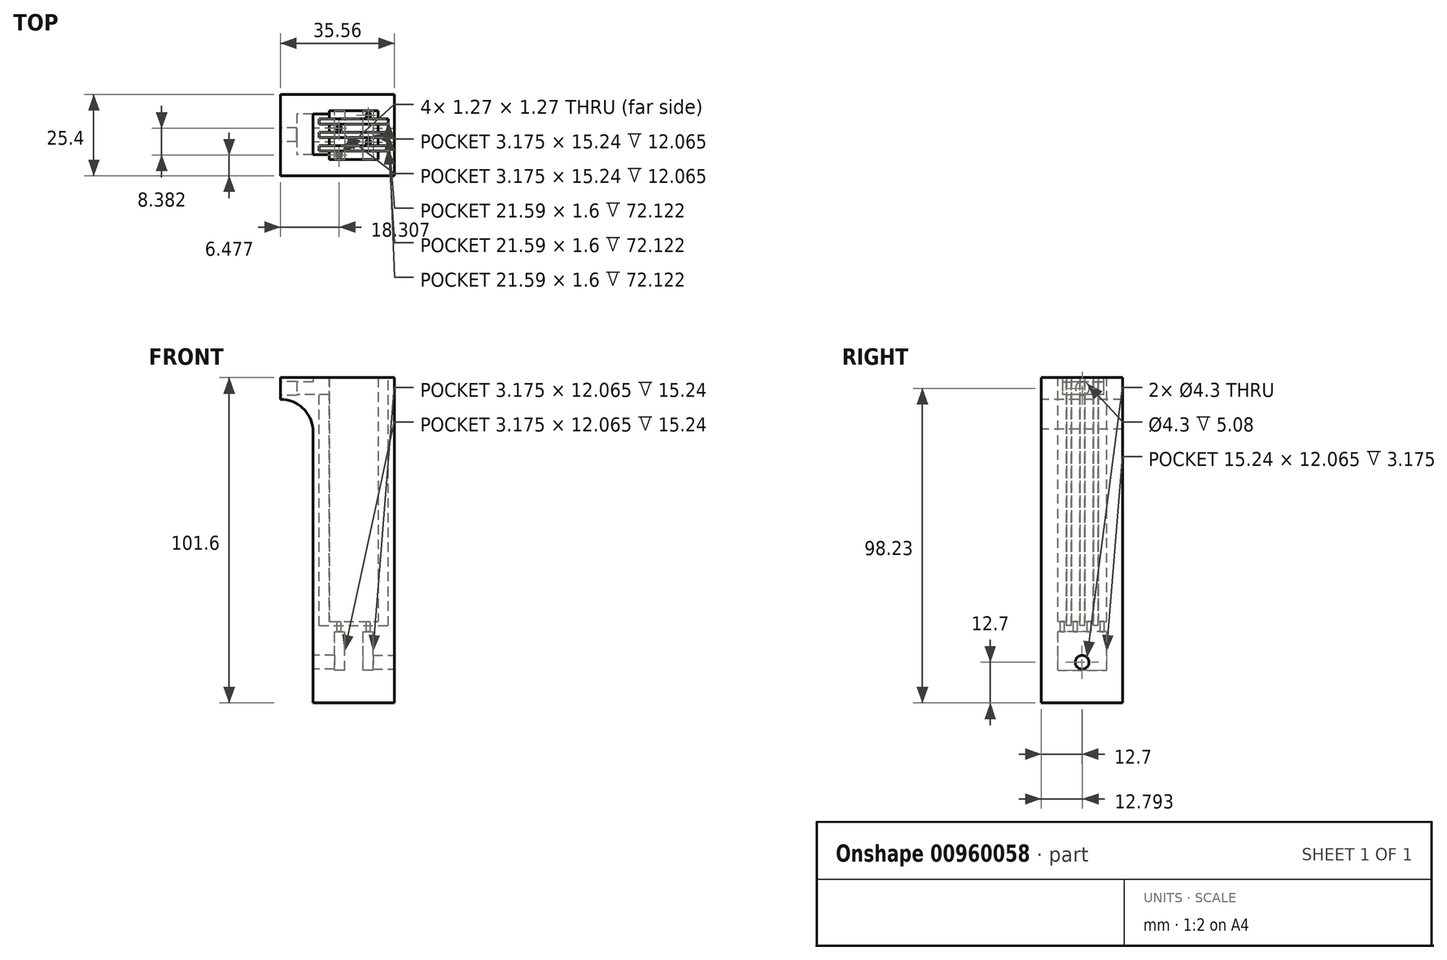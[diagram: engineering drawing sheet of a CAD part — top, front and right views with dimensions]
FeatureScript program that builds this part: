
annotation { "Feature Type Name" : "Feature", "Feature Type Description" : "" }
export const myFeature = defineFeature(function(context is Context, id is Id, definition is map)
    precondition{}
    {
        {
            var Q0;
            Q0=qCreatedBy(makeId("Top.planeOp"),FACE);
            var sketch = newSketch(context, id + "F0", { "sketchPlane" : qUnion([Q0])});
            skLineSegment(sketch, "E0.bottom", {"start": v(0, 0) * mm, "end": v(25.4, 0) * mm});
            skLineSegment(sketch, "E0.top", {"start": v(0, 25.4) * mm, "end": v(25.4, 25.4) * mm});
            skLineSegment(sketch, "E0.left", {"start": v(0, 0) * mm, "end": v(0, 25.4) * mm});
            skLineSegment(sketch, "E0.right", {"start": v(25.4, 0) * mm, "end": v(25.4, 25.4) * mm});
            skSolve(sketch);
        }
        {
            var Q0;
            Q0=makeQuery(id+"F0.imprint","IMPRINT",FACE,{"disambiguationData":[TD([[makeQuery(id+"F0.imprint","IMPRINT",EDGE,{"derivedFrom":sQuery(id+"F0.wireOp",EDGE,"E0.bottom")}),1.0]])]});
            extrude(context, id + "F1", {"entities" : qUnion([Q0]), "depth" : 101.6 * mm, "offsetDistance" : 25.4 * mm});
        }
        {
            var Q0;
            Q0=makeQuery(id+"F1.opExtrude","CAP_FACE",FACE,{"disambiguationData":[OSD([sQuery(id+"F0.wireOp",EDGE,"E0.bottom"),sQuery(id+"F0.wireOp",EDGE,"E0.top"),sQuery(id+"F0.wireOp",EDGE,"E0.left"),sQuery(id+"F0.wireOp",EDGE,"E0.right")])],"isStart":false});
            var sketch = newSketch(context, id + "F2", { "sketchPlane" : qUnion([Q0])});
            skLineSegment(sketch, "E1.bottom", {"start": v(5.08, 5.08) * mm, "end": v(20.32, 5.08) * mm});
            skLineSegment(sketch, "E1.top", {"start": v(5.08, 20.32) * mm, "end": v(20.32, 20.32) * mm});
            skLineSegment(sketch, "E1.left", {"start": v(5.08, 5.08) * mm, "end": v(5.08, 20.32) * mm});
            skLineSegment(sketch, "E1.right", {"start": v(20.32, 5.08) * mm, "end": v(20.32, 20.32) * mm});
            skSolve(sketch);
        }
        {
            var Q0;
            Q0=makeQuery(id+"F2.imprint","IMPRINT",FACE,{"disambiguationData":[TD([[makeQuery(id+"F2.imprint","IMPRINT",EDGE,{"derivedFrom":sQuery(id+"F2.wireOp",EDGE,"E1.bottom")}),1.0]])]});
            extrude(context, id + "F3", {"entities" : qUnion([Q0]), "operationType" : NewBodyOperationType.REMOVE, "oppositeDirection" : true, "depth" : 76.2 * mm, "offsetDistance" : 25.4 * mm});
        }
        {
            var Q0;
            Q0=makeQuery(id+"F1.opExtrude","SWEPT_FACE",FACE,{"disambiguationData":[OSD([sQuery(id+"F0.wireOp",EDGE,"E0.right")])]});
            var sketch = newSketch(context, id + "F4", { "sketchPlane" : qUnion([Q0])});
            skCircle(sketch, "E2", {"center": v(12.7, 12.7) * mm, "radius": 2.15 * mm});
            skSolve(sketch);
        }
        {
            var Q0;
            Q0=makeQuery(id+"F3.boolean.opBoolean","COPY",FACE,{"derivedFrom":makeQuery(id+"F3.opExtrude","CAP_FACE",FACE,{"disambiguationData":[OSD([sQuery(id+"F2.wireOp",EDGE,"E1.bottom"),sQuery(id+"F2.wireOp",EDGE,"E1.top"),sQuery(id+"F2.wireOp",EDGE,"E1.left"),sQuery(id+"F2.wireOp",EDGE,"E1.right")])],"isStart":false})});
            var sketch = newSketch(context, id + "F5", { "sketchPlane" : qUnion([Q0])});
            skLineSegment(sketch, "E3.bottom", {"start": v(15.56, 20.32) * mm, "end": v(18.73, 20.32) * mm});
            skLineSegment(sketch, "E3.top", {"start": v(15.56, 5.08) * mm, "end": v(18.73, 5.08) * mm});
            skLineSegment(sketch, "E3.left", {"start": v(15.56, 20.32) * mm, "end": v(15.56, 5.08) * mm});
            skLineSegment(sketch, "E3.right", {"start": v(18.73, 20.32) * mm, "end": v(18.73, 5.08) * mm});
            skLineSegment(sketch, "E4.bottom", {"start": v(6.67, 20.32) * mm, "end": v(9.84, 20.32) * mm});
            skLineSegment(sketch, "E4.top", {"start": v(6.67, 5.08) * mm, "end": v(9.84, 5.08) * mm});
            skLineSegment(sketch, "E4.left", {"start": v(6.67, 20.32) * mm, "end": v(6.67, 5.08) * mm});
            skLineSegment(sketch, "E4.right", {"start": v(9.84, 20.32) * mm, "end": v(9.84, 5.08) * mm});
            skSolve(sketch);
        }
        {
            var Q0;
            Q0=qSketchRegion(id+"F5",true);
            extrude(context, id + "F6", {"entities" : qUnion([Q0]), "operationType" : NewBodyOperationType.REMOVE, "endBound" : BoundingType.UP_TO_NEXT, "oppositeDirection" : true, "depth" : 25.4 * mm, "hasOffset" : true, "offsetDistance" : 10.16 * mm, "hasSecondDirection" : true, "secondDirectionOppositeDirection" : false, "secondDirectionDepth" : -3.17 * mm});
        }
        {
            var Q0;
            Q0=qSketchRegion(id+"F4",true);
            extrude(context, id + "F7", {"entities" : qUnion([Q0]), "operationType" : NewBodyOperationType.REMOVE, "endBound" : BoundingType.UP_TO_NEXT, "oppositeDirection" : true, "depth" : 25.4 * mm, "offsetDistance" : 25.4 * mm});
        }
        {
            var Q0;
            Q0=makeQuery(id+"F1.opExtrude","SWEPT_FACE",FACE,{"disambiguationData":[OSD([sQuery(id+"F0.wireOp",EDGE,"E0.left")])]});
            var sketch = newSketch(context, id + "F8", { "sketchPlane" : qUnion([Q0])});
            skCircle(sketch, "E5", {"center": v(-12.7, 12.7) * mm, "radius": 2.15 * mm});
            skSolve(sketch);
        }
        {
            var Q0;
            Q0=qSketchRegion(id+"F8",true);
            extrude(context, id + "F9", {"entities" : qUnion([Q0]), "operationType" : NewBodyOperationType.REMOVE, "endBound" : BoundingType.UP_TO_NEXT, "oppositeDirection" : true, "depth" : 25.4 * mm, "offsetDistance" : 25.4 * mm});
        }
        {
            var Q0;
            Q0=makeQuery(id+"F3.boolean.opBoolean","COPY",FACE,{"derivedFrom":makeQuery(id+"F3.opExtrude","CAP_FACE",FACE,{"disambiguationData":[OSD([sQuery(id+"F2.wireOp",EDGE,"E1.bottom"),sQuery(id+"F2.wireOp",EDGE,"E1.top"),sQuery(id+"F2.wireOp",EDGE,"E1.left"),sQuery(id+"F2.wireOp",EDGE,"E1.right")])],"isStart":false})});
            var sketch = newSketch(context, id + "F10", { "sketchPlane" : qUnion([Q0])});
            skLineSegment(sketch, "E6.bottom", {"start": v(16.57, 19.56) * mm, "end": v(17.84, 19.56) * mm});
            skLineSegment(sketch, "E6.top", {"start": v(16.57, 18.29) * mm, "end": v(17.84, 18.29) * mm});
            skLineSegment(sketch, "E6.left", {"start": v(16.57, 19.56) * mm, "end": v(16.57, 18.29) * mm});
            skLineSegment(sketch, "E6.right", {"start": v(17.84, 19.56) * mm, "end": v(17.84, 18.29) * mm});
            skLineSegment(sketch, "E7.0.1.0", {"start": v(16.57, 11.18) * mm, "end": v(17.84, 11.18) * mm});
            skLineSegment(sketch, "E7.0.1.1", {"start": v(17.84, 11.18) * mm, "end": v(17.84, 9.9) * mm});
            skLineSegment(sketch, "E7.0.1.2", {"start": v(16.57, 9.9) * mm, "end": v(17.84, 9.9) * mm});
            skLineSegment(sketch, "E7.0.1.3", {"start": v(16.57, 11.18) * mm, "end": v(16.57, 9.9) * mm});
            skLineSegment(sketch, "E7.direction1", {"start": v(16.57, 18.29) * mm, "end": v(41.97, 18.29) * mm, "construction": true});
            skLineSegment(sketch, "E7.direction2", {"start": v(16.57, 18.29) * mm, "end": v(16.57, 9.9) * mm, "construction": true});
            skSolve(sketch);
        }
        {
            var Q0;
            Q0=makeQuery(id+"F10.imprint","IMPRINT",FACE,{"disambiguationData":[TD([[makeQuery(id+"F10.imprint","IMPRINT",EDGE,{"derivedFrom":sQuery(id+"F10.wireOp",EDGE,"E6.bottom")}),1.0]])]});
            var sketch = newSketch(context, id + "F11", { "sketchPlane" : qUnion([Q0])});
            skLineSegment(sketch, "E8.bottom", {"start": v(7.51, 7.11) * mm, "end": v(8.78, 7.11) * mm});
            skLineSegment(sketch, "E8.top", {"start": v(7.51, 5.84) * mm, "end": v(8.78, 5.84) * mm});
            skLineSegment(sketch, "E8.left", {"start": v(7.51, 7.11) * mm, "end": v(7.51, 5.84) * mm});
            skLineSegment(sketch, "E8.right", {"start": v(8.78, 7.11) * mm, "end": v(8.78, 5.84) * mm});
            skLineSegment(sketch, "E9.bottom", {"start": v(7.51, 15.5) * mm, "end": v(8.78, 15.5) * mm});
            skLineSegment(sketch, "E9.top", {"start": v(7.51, 14.22) * mm, "end": v(8.78, 14.22) * mm});
            skLineSegment(sketch, "E9.left", {"start": v(7.51, 15.5) * mm, "end": v(7.51, 14.22) * mm});
            skLineSegment(sketch, "E9.right", {"start": v(8.78, 15.5) * mm, "end": v(8.78, 14.22) * mm});
            skSolve(sketch);
        }
        {
            var Q0;
            Q0=qSketchRegion(id+"F10",true);
            extrude(context, id + "F12", {"entities" : qUnion([Q0]), "operationType" : NewBodyOperationType.REMOVE, "endBound" : BoundingType.UP_TO_NEXT, "oppositeDirection" : true, "depth" : 25.4 * mm, "offsetDistance" : 25.4 * mm});
        }
        {
            var Q0;
            Q0=qSketchRegion(id+"F11",true);
            extrude(context, id + "F13", {"entities" : qUnion([Q0]), "operationType" : NewBodyOperationType.REMOVE, "endBound" : BoundingType.UP_TO_NEXT, "oppositeDirection" : true, "depth" : 25.4 * mm, "offsetDistance" : 25.4 * mm});
        }
        {
            var Q0;
            Q0=makeQuery(id+"F1.opExtrude","SWEPT_FACE",FACE,{"disambiguationData":[OSD([sQuery(id+"F0.wireOp",EDGE,"E0.left")])]});
            var sketch = newSketch(context, id + "F14", { "sketchPlane" : qUnion([Q0])});
            skLineSegment(sketch, "E10.bottom", {"start": v(-19.33, 100.27) * mm, "end": v(-6.55, 100.27) * mm});
            skLineSegment(sketch, "E10.top", {"start": v(-19.33, 96.25) * mm, "end": v(-6.55, 96.25) * mm});
            skLineSegment(sketch, "E10.left", {"start": v(-19.33, 100.27) * mm, "end": v(-19.33, 96.25) * mm});
            skLineSegment(sketch, "E10.right", {"start": v(-6.55, 100.27) * mm, "end": v(-6.55, 96.25) * mm});
            skSolve(sketch);
        }
        {
            var Q0;
            Q0=qSketchRegion(id+"F14",true);
            extrude(context, id + "F15", {"entities" : qUnion([Q0]), "operationType" : NewBodyOperationType.REMOVE, "endBound" : BoundingType.UP_TO_NEXT, "oppositeDirection" : true, "depth" : 25.4 * mm, "offsetDistance" : 25.4 * mm});
        }
        {
            var Q0;
            Q0=makeQuery(id+"F1.opExtrude","SWEPT_FACE",FACE,{"disambiguationData":[OSD([sQuery(id+"F0.wireOp",EDGE,"E0.left")])]});
            var sketch = newSketch(context, id + "F16", { "sketchPlane" : qUnion([Q0])});
            skLineSegment(sketch, "E11.bottom", {"start": v(-25.4, 101.6) * mm, "end": v(0, 101.6) * mm});
            skLineSegment(sketch, "E11.top", {"start": v(-25.4, 94.82) * mm, "end": v(0, 94.82) * mm});
            skLineSegment(sketch, "E11.left", {"start": v(-25.4, 101.6) * mm, "end": v(-25.4, 94.82) * mm});
            skLineSegment(sketch, "E11.right", {"start": v(0, 101.6) * mm, "end": v(0, 94.82) * mm});
            skSolve(sketch);
        }
        {
            var Q0;
            Q0=makeQuery(id+"F16.imprint","IMPRINT",FACE,{"disambiguationData":[TD([[makeQuery(id+"F16.imprint","IMPRINT",EDGE,{"derivedFrom":sQuery(id+"F16.wireOp",EDGE,"E11.bottom")}),1.0]])]});
            extrude(context, id + "F17", {"entities" : qUnion([Q0]), "operationType" : NewBodyOperationType.ADD, "depth" : 5.08 * mm, "offsetDistance" : 25.4 * mm});
        }
        {
            var Q0;
            Q0=makeQuery(id+"F17.opExtrude","CAP_FACE",FACE,{"disambiguationData":[OSD([sQuery(id+"F14.wireOp",EDGE,"E10.bottom"),sQuery(id+"F14.wireOp",EDGE,"E10.top"),sQuery(id+"F14.wireOp",EDGE,"E10.left"),sQuery(id+"F14.wireOp",EDGE,"E10.right"),sQuery(id+"F16.wireOp",EDGE,"E11.bottom"),sQuery(id+"F16.wireOp",EDGE,"E11.top"),sQuery(id+"F16.wireOp",EDGE,"E11.left"),sQuery(id+"F16.wireOp",EDGE,"E11.right")])],"isStart":false});
            var sketch = newSketch(context, id + "F18", { "sketchPlane" : qUnion([Q0])});
            skLineSegment(sketch, "E12.bottom", {"start": v(-25.4, 101.6) * mm, "end": v(0, 101.6) * mm});
            skLineSegment(sketch, "E12.top", {"start": v(-25.4, 94.82) * mm, "end": v(0, 94.82) * mm});
            skLineSegment(sketch, "E12.left", {"start": v(-25.4, 101.6) * mm, "end": v(-25.4, 94.82) * mm});
            skLineSegment(sketch, "E12.right", {"start": v(0, 101.6) * mm, "end": v(0, 94.82) * mm});
            skSolve(sketch);
        }
        {
            var Q0;
            Q0=qSketchRegion(id+"F18",true);
            extrude(context, id + "F19", {"entities" : qUnion([Q0]), "operationType" : NewBodyOperationType.ADD, "depth" : 5.08 * mm, "offsetDistance" : 25.4 * mm});
        }
        {
            var Q0;
            Q0=makeQuery(id+"F19.opExtrude","CAP_FACE",FACE,{"disambiguationData":[OSD([sQuery(id+"F18.wireOp",EDGE,"E12.bottom"),sQuery(id+"F18.wireOp",EDGE,"E12.top"),sQuery(id+"F18.wireOp",EDGE,"E12.left"),sQuery(id+"F18.wireOp",EDGE,"E12.right")])],"isStart":false});
            var sketch = newSketch(context, id + "F20", { "sketchPlane" : qUnion([Q0])});
            skCircle(sketch, "E13", {"center": v(-12.8, 98.23) * mm, "radius": 2.15 * mm});
            skSolve(sketch);
        }
        {
            var Q0;
            Q0=qSketchRegion(id+"F20",true);
            extrude(context, id + "F21", {"entities" : qUnion([Q0]), "operationType" : NewBodyOperationType.REMOVE, "oppositeDirection" : true, "depth" : 5.08 * mm, "offsetDistance" : 25.4 * mm});
        }
        {
            var Q0;
            Q0=makeQuery(id+"F19.boolean.opBoolean","MERGE",FACE,{"derivedFrom":[makeQuery(id+"F17.boolean.opBoolean","MERGE",FACE,{"derivedFrom":[makeQuery(id+"F1.opExtrude","SWEPT_FACE",FACE,{"disambiguationData":[OSD([sQuery(id+"F0.wireOp",EDGE,"E0.bottom")])]}),makeQuery(id+"F17.opExtrude","SWEPT_FACE",FACE,{"disambiguationData":[OSD([sQuery(id+"F16.wireOp",EDGE,"E11.right")])]})]}),makeQuery(id+"F19.opExtrude","SWEPT_FACE",FACE,{"disambiguationData":[OSD([sQuery(id+"F18.wireOp",EDGE,"E12.right")])]})]});
            var sketch = newSketch(context, id + "F22", { "sketchPlane" : qUnion([Q0])});
            skArc(sketch, "E14", {"start": v(0, 85.44) * mm, "mid": v(-3.25, 92.12) * mm, "end": v(-10.16, 94.82) * mm});
            skLineSegment(sketch, "E15", {"start": v(-10.16, 94.82) * mm, "end": v(0, 94.82) * mm});
            skLineSegment(sketch, "E16", {"start": v(0, 94.82) * mm, "end": v(0, 85.44) * mm});
            skSolve(sketch);
        }
        {
            var Q0;
            Q0 = qSketchRegion(id + "F22", true);
            var Q1;
            Q1=makeQuery(id+"F19.boolean.opBoolean","MERGE",FACE,{"derivedFrom":[makeQuery(id+"F17.boolean.opBoolean","MERGE",FACE,{"derivedFrom":[makeQuery(id+"F1.opExtrude","SWEPT_FACE",FACE,{"disambiguationData":[OSD([sQuery(id+"F0.wireOp",EDGE,"E0.top")])]}),makeQuery(id+"F17.opExtrude","SWEPT_FACE",FACE,{"disambiguationData":[OSD([sQuery(id+"F16.wireOp",EDGE,"E11.left")])]})]}),makeQuery(id+"F19.opExtrude","SWEPT_FACE",FACE,{"disambiguationData":[OSD([sQuery(id+"F18.wireOp",EDGE,"E12.left")])]})]});
            extrude(context, id + "F23", {"entities" : qUnion([Q0]), "operationType" : NewBodyOperationType.ADD, "endBound" : BoundingType.UP_TO_SURFACE, "oppositeDirection" : true, "depth" : 25.4 * mm, "endBoundEntityFace" : qUnion([Q1]), "offsetDistance" : 25.4 * mm});
        }
        {
            var Q0;
            Q0=makeQuery(id+"F19.boolean.opBoolean","MERGE",FACE,{"derivedFrom":[makeQuery(id+"F17.boolean.opBoolean","MERGE",FACE,{"derivedFrom":[makeQuery(id+"F1.opExtrude","CAP_FACE",FACE,{"disambiguationData":[OSD([sQuery(id+"F0.wireOp",EDGE,"E0.bottom"),sQuery(id+"F0.wireOp",EDGE,"E0.top"),sQuery(id+"F0.wireOp",EDGE,"E0.left"),sQuery(id+"F0.wireOp",EDGE,"E0.right")])],"isStart":false}),makeQuery(id+"F17.opExtrude","SWEPT_FACE",FACE,{"disambiguationData":[OSD([sQuery(id+"F16.wireOp",EDGE,"E11.bottom")])]})]}),makeQuery(id+"F19.opExtrude","SWEPT_FACE",FACE,{"disambiguationData":[OSD([sQuery(id+"F18.wireOp",EDGE,"E12.bottom")])]})]});
            var sketch = newSketch(context, id + "F24", { "sketchPlane" : qUnion([Q0])});
            skLineSegment(sketch, "E17.bottom", {"start": v(1.9, 17.74) * mm, "end": v(23.5, 17.74) * mm});
            skLineSegment(sketch, "E17.top", {"start": v(1.9, 16.14) * mm, "end": v(23.5, 16.14) * mm});
            skLineSegment(sketch, "E17.left", {"start": v(1.9, 17.74) * mm, "end": v(1.9, 16.14) * mm});
            skLineSegment(sketch, "E17.right", {"start": v(23.5, 17.74) * mm, "end": v(23.5, 16.14) * mm});
            skLineSegment(sketch, "E18.bottom", {"start": v(1.9, 9.37) * mm, "end": v(23.5, 9.37) * mm});
            skLineSegment(sketch, "E18.top", {"start": v(1.9, 7.77) * mm, "end": v(23.5, 7.77) * mm});
            skLineSegment(sketch, "E18.left", {"start": v(1.9, 9.37) * mm, "end": v(1.9, 7.77) * mm});
            skLineSegment(sketch, "E18.right", {"start": v(23.5, 9.37) * mm, "end": v(23.5, 7.77) * mm});
            skLineSegment(sketch, "E19.bottom", {"start": v(1.9, 13.55) * mm, "end": v(23.5, 13.55) * mm});
            skLineSegment(sketch, "E19.top", {"start": v(1.9, 11.95) * mm, "end": v(23.5, 11.95) * mm});
            skLineSegment(sketch, "E19.left", {"start": v(1.9, 13.55) * mm, "end": v(1.9, 11.95) * mm});
            skLineSegment(sketch, "E19.right", {"start": v(23.5, 13.55) * mm, "end": v(23.5, 11.95) * mm});
            skSolve(sketch);
        }
        {
            var Q0;
            Q0 = qSketchRegion(id + "F24", true);
            extrude(context, id + "F25", {"entities" : qUnion([Q0]), "operationType" : NewBodyOperationType.REMOVE, "oppositeDirection" : true, "depth" : 77.47 * mm, "offsetDistance" : 25.4 * mm});
        }
        {
            var Q0;
            {var subQ0=sQuery(id+"F14.wireOp",EDGE,"E10.bottom");Q0=makeQuery(id+"F25.boolean.opBoolean","SPLIT",FACE,{"disambiguationData":[TD([makeQuery(id+"F1.opExtrude","CAP_FACE",FACE,{"disambiguationData":[OSD([sQuery(id+"F0.wireOp",EDGE,"E0.bottom"),sQuery(id+"F0.wireOp",EDGE,"E0.top"),sQuery(id+"F0.wireOp",EDGE,"E0.left"),sQuery(id+"F0.wireOp",EDGE,"E0.right")])],"isStart":false}),makeQuery(id+"F15.boolean.opBoolean","COPY",FACE,{"derivedFrom":makeQuery(id+"F15.opExtrude","SWEPT_FACE",FACE,{"disambiguationData":[OSD([subQ0])]})}),makeQuery(id+"F17.opExtrude","SWEPT_FACE",FACE,{"disambiguationData":[OSD([sQuery(id+"F16.wireOp",EDGE,"E11.bottom")])]}),makeQuery(id+"F17.opExtrude","SWEPT_FACE",FACE,{"disambiguationData":[OSD([subQ0])]}),makeQuery(id+"F19.opExtrude","SWEPT_FACE",FACE,{"disambiguationData":[OSD([sQuery(id+"F18.wireOp",EDGE,"E12.bottom")])]}),makeQuery(id+"F25.opExtrude","SWEPT_FACE",FACE,{"disambiguationData":[OSD([sQuery(id+"F24.wireOp",EDGE,"E18.top")])]}),makeQuery(id+"F25.opExtrude","SWEPT_FACE",FACE,{"disambiguationData":[OSD([sQuery(id+"F24.wireOp",EDGE,"932b69c3-4fd8-45e5-8434-84e7324a444d.bottom")])]})])],"derivedFrom":makeQuery(id+"F3.boolean.opBoolean","COPY",FACE,{"derivedFrom":makeQuery(id+"F3.opExtrude","SWEPT_FACE",FACE,{"disambiguationData":[OSD([sQuery(id+"F2.wireOp",EDGE,"E1.left")])]})})});}
            var sketch = newSketch(context, id + "F26", { "sketchPlane" : qUnion([Q0])});
            skLineSegment(sketch, "E20.bottom", {"start": v(6.55, 101.6) * mm, "end": v(19.33, 101.6) * mm});
            skLineSegment(sketch, "E20.top", {"start": v(6.55, 100.27) * mm, "end": v(19.33, 100.27) * mm});
            skLineSegment(sketch, "E20.left", {"start": v(6.55, 101.6) * mm, "end": v(6.55, 100.27) * mm});
            skLineSegment(sketch, "E20.right", {"start": v(19.33, 101.6) * mm, "end": v(19.33, 100.27) * mm});
            skSolve(sketch);
        }
        {
            var Q0;
            Q0 = qSketchRegion(id + "F26", true);
            var Q1;
            {var subQ0=sQuery(id+"F14.wireOp",EDGE,"E10.bottom");Q1=makeQuery(id+"F25.boolean.opBoolean","COPY",FACE,{"disambiguationData":[TD([makeQuery(id+"F15.boolean.opBoolean","COPY",FACE,{"derivedFrom":makeQuery(id+"F15.opExtrude","SWEPT_FACE",FACE,{"disambiguationData":[OSD([subQ0])]})})])],"derivedFrom":makeQuery(id+"F25.opExtrude","SWEPT_FACE",FACE,{"disambiguationData":[OSD([sQuery(id+"F24.wireOp",EDGE,"E18.left")])]})});}
            extrude(context, id + "F27", {"entities" : qUnion([Q0]), "operationType" : NewBodyOperationType.REMOVE, "oppositeDirection" : true, "depth" : 5.08 * mm, "endBoundEntityFace" : qUnion([Q1]), "offsetDistance" : 25.4 * mm});
        }
    });
